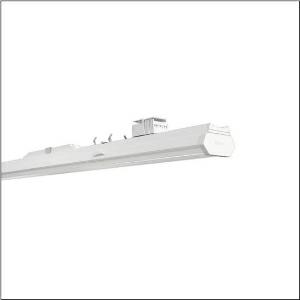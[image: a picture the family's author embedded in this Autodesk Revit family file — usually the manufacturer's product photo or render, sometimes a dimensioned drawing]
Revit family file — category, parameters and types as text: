
# Revit family: licross_r__21_protected_mo_52td12dne75f_b15f
name_source: partatom
category: Lighting Fixtures
units: mm (PartAtom-declared; Revit-internal decimal feet)

## family parameters
Cut with Voids When Loaded = No
Host = Face
Light Source = No
Part Type = Normal
Room Calculation Point = No
Round Connector Dimension = Use Diameter
Shared = No

## types (1)
- --- (1 x LED, 7720 lm, 61 W, 5000K)
    Apparent Load = 61 VA
    CIE Flux Codes = 73 92 98 99 100
    Color Rendering = 90
    Color Temperature = 5000K
    Default Elevation = 1800 mm
    Description = Licross® 21 Protected MOluminaire insert, length: 1.500mm, width: 90mm, height: 103mm, LED rated luminous flux: 7.720lm, light colour: 950, control gear: DALI 2, control gear: ECG DALI, with plug, 5-pole, with phase selection, mains connection: 220..240V, AC, 50/60Hz, halogen-free wiring, primary optical cover: cover, of PMMA, light emission: direct with ceiling illumination distribution, protection rating (complete): IP54, insulation class (complete): insulation class I (protective earthing), certification: CE, ENEC, VDE, UKCA, protection symbol: D if used in an environment with non-conductive dust loads with corresponding accessories, permissible ambient temperature for indoor applications: -25..+40°C, corresponds to IFS (International Featured Standards) requirements for safety and quality in the food industry, reducing of maximum allowable ambient temperature of 5°C with ceiling mounting, packaging unit: 1 piece
    Height = 92 mm
    Lamp = 1 x LED
    Lamp Light Flux = 7720 lm
    Lamp Power = 61 W
    Lamp count = 1
    Length = 1500 mm
    Luminous efficacy = 127 lm/W
    Manufacturer = Siteco
    ModVariant = No
    Model = 52TD12DNE75F
    Mounting Place = Ceiling
    Mounting Type = Pendant
    Number of Poles = 1
    OnlyDefault = Yes
    Power Factor = 1
    Product Name = Licross® 21 Protected MO
    Product group = luminaire insert
    ProductGroupID = 902
    Protection Class = Protection class I
    Protection Degree = IP 54
    RLX_Detail_Level = 1
    RlxData = <blob elided: 24205 chars, md5=bfdd515a>
    Socket = socket
    Standby Power = 0 W
    System Light Flux = 7720 lm
    System Power = 61 W
    Type Comments = factory setting: luminous flux: 100 % | dim-lin: 254 | 405 mA
    Type Image = l_1256148.jpg
    URL = http://relux.com
    VarID = @adj_129323
    Voltage = 0 V
    Weight = 0.00 kg
    Width = 88 mm

## geometry (parser evidence)
native form markers: Blend x4, Sweep x12
no freeform markers — native parametric forms only
